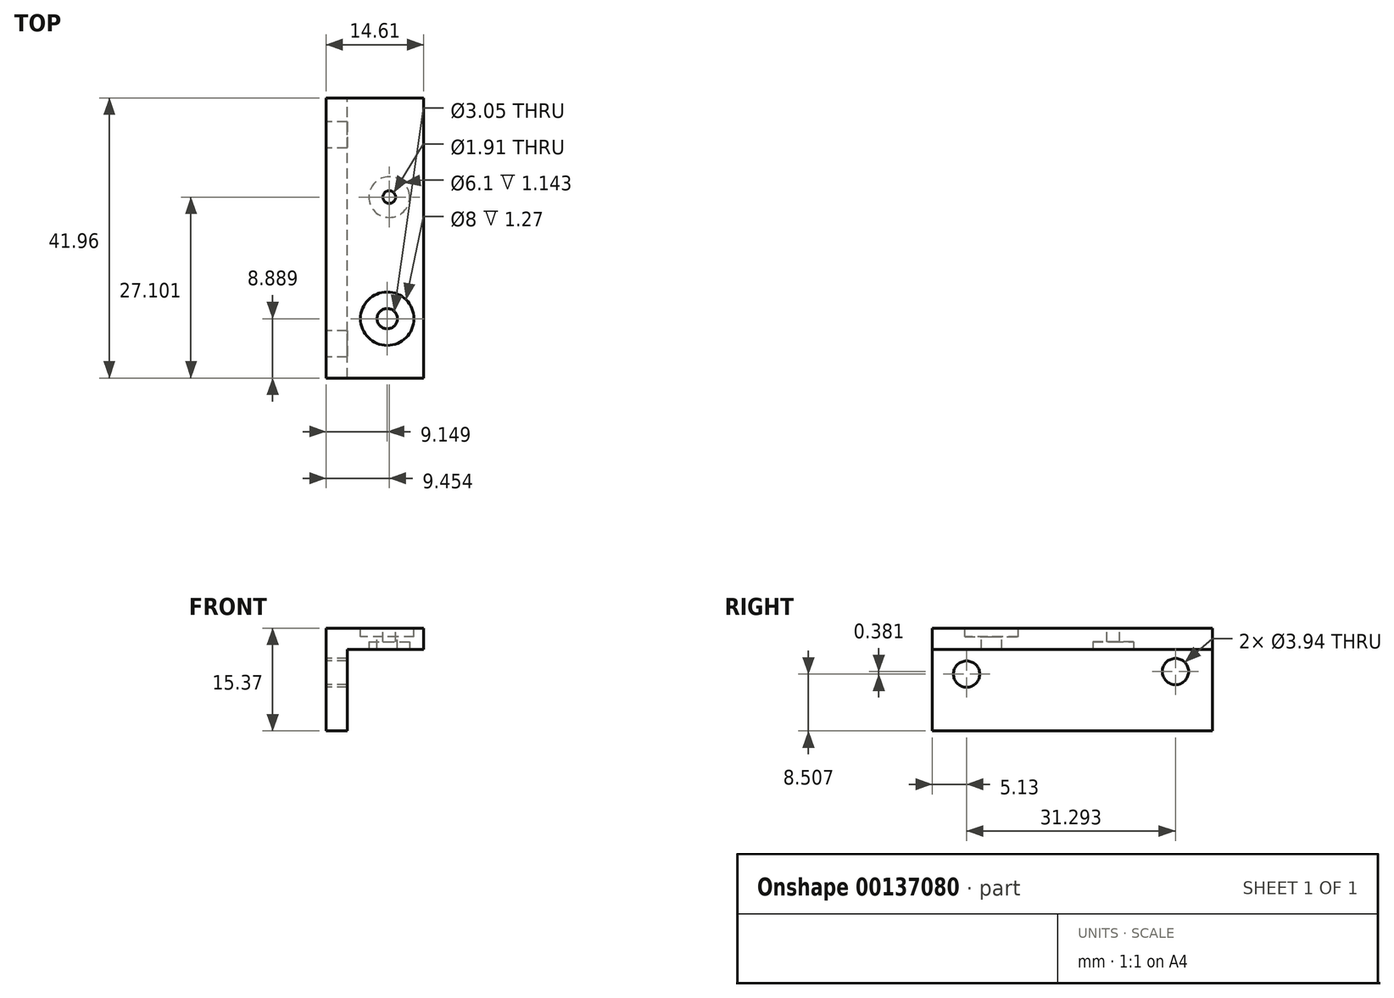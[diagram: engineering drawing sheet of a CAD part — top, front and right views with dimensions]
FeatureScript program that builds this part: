
annotation { "Feature Type Name" : "Feature", "Feature Type Description" : "" }
export const myFeature = defineFeature(function(context is Context, id is Id, definition is map)
    precondition{}
    {
        {
            var Q0;
            Q0=qCreatedBy(makeId("Front.planeOp"),FACE);
            var sketch = newSketch(context, id + "F0", { "sketchPlane" : qUnion([Q0])});
            skLineSegment(sketch, "E0", {"start": v(0, 0) * mm, "end": v(11.43, 0) * mm});
            skLineSegment(sketch, "E1", {"start": v(11.43, 0) * mm, "end": v(11.43, 3.18) * mm});
            skLineSegment(sketch, "E2", {"start": v(11.43, 3.18) * mm, "end": v(-3.18, 3.17) * mm});
            skLineSegment(sketch, "E3", {"start": v(-3.18, 3.17) * mm, "end": v(-3.17, -12.2) * mm});
            skLineSegment(sketch, "E4", {"start": v(-3.17, -12.2) * mm, "end": v(0, -12.2) * mm});
            skLineSegment(sketch, "E5", {"start": v(0, -12.2) * mm, "end": v(0, 0) * mm});
            skSolve(sketch);
        }
        {
            var Q0;
            Q0 = qSketchRegion(id + "F0", true);
            extrude(context, id + "F1", {"entities" : qUnion([Q0]), "depth" : 41.96 * mm});
        }
        {
            var Q0;
            Q0=makeQuery(id+"F1.opExtrude","SWEPT_FACE",FACE,{"disambiguationData":[OSD([sQuery(id+"F0.wireOp",EDGE,"E3")])]});
            var sketch = newSketch(context, id + "F2", { "sketchPlane" : qUnion([Q0])});
            skCircle(sketch, "E6", {"center": v(5.54, -3.3) * mm, "radius": 1.97 * mm});
            skCircle(sketch, "E7", {"center": v(36.83, -3.68) * mm, "radius": 1.97 * mm});
            skSolve(sketch);
        }
        {
            var Q0;
            Q0 = qSketchRegion(id + "F2", true);
            extrude(context, id + "F3", {"entities" : qUnion([Q0]), "operationType" : NewBodyOperationType.REMOVE, "endBound" : BoundingType.THROUGH_ALL, "oppositeDirection" : true, "depth" : 25.4 * mm});
        }
        {
            var Q0;
            Q0=makeQuery(id+"F1.opExtrude","SWEPT_FACE",FACE,{"disambiguationData":[OSD([sQuery(id+"F0.wireOp",EDGE,"E2")])]});
            var sketch = newSketch(context, id + "F4", { "sketchPlane" : qUnion([Q0])});
            skCircle(sketch, "E8", {"center": v(6.27, -14.86) * mm, "radius": 0.95 * mm});
            skSolve(sketch);
        }
        {
            var Q0;
            Q0 = qSketchRegion(id + "F4", true);
            extrude(context, id + "F5", {"entities" : qUnion([Q0]), "operationType" : NewBodyOperationType.REMOVE, "endBound" : BoundingType.THROUGH_ALL, "oppositeDirection" : true, "depth" : 25.4 * mm});
        }
        {
            var Q0;
            Q0=makeQuery(id+"F1.opExtrude","SWEPT_FACE",FACE,{"disambiguationData":[OSD([sQuery(id+"F0.wireOp",EDGE,"E0")])]});
            var sketch = newSketch(context, id + "F6", { "sketchPlane" : qUnion([Q0])});
            skCircle(sketch, "E9", {"center": v(6.27, 14.86) * mm, "radius": 3.05 * mm});
            skSolve(sketch);
        }
        {
            var Q0;
            Q0 = qSketchRegion(id + "F6", true);
            extrude(context, id + "F7", {"entities" : qUnion([Q0]), "operationType" : NewBodyOperationType.REMOVE, "oppositeDirection" : true, "depth" : 1.14 * mm});
        }
        {
            var Q0;
            Q0=makeQuery(id+"F1.opExtrude","SWEPT_FACE",FACE,{"disambiguationData":[OSD([sQuery(id+"F0.wireOp",EDGE,"E2")])]});
            var sketch = newSketch(context, id + "F8", { "sketchPlane" : qUnion([Q0])});
            skCircle(sketch, "E10", {"center": v(5.97, -33.07) * mm, "radius": 1.52 * mm});
            skSolve(sketch);
        }
        {
            var Q0;
            Q0 = qSketchRegion(id + "F8", true);
            extrude(context, id + "F9", {"entities" : qUnion([Q0]), "operationType" : NewBodyOperationType.REMOVE, "endBound" : BoundingType.THROUGH_ALL, "oppositeDirection" : true, "depth" : 25.4 * mm});
        }
        {
            var Q0;
            Q0=makeQuery(id+"F1.opExtrude","SWEPT_FACE",FACE,{"disambiguationData":[OSD([sQuery(id+"F0.wireOp",EDGE,"E2")])]});
            var sketch = newSketch(context, id + "F10", { "sketchPlane" : qUnion([Q0])});
            skCircle(sketch, "E11", {"center": v(5.97, -33.07) * mm, "radius": 4 * mm});
            skSolve(sketch);
        }
        {
            var Q0;
            Q0 = qSketchRegion(id + "F10", true);
            extrude(context, id + "F11", {"entities" : qUnion([Q0]), "operationType" : NewBodyOperationType.REMOVE, "oppositeDirection" : true, "depth" : 1.27 * mm});
        }
    });
